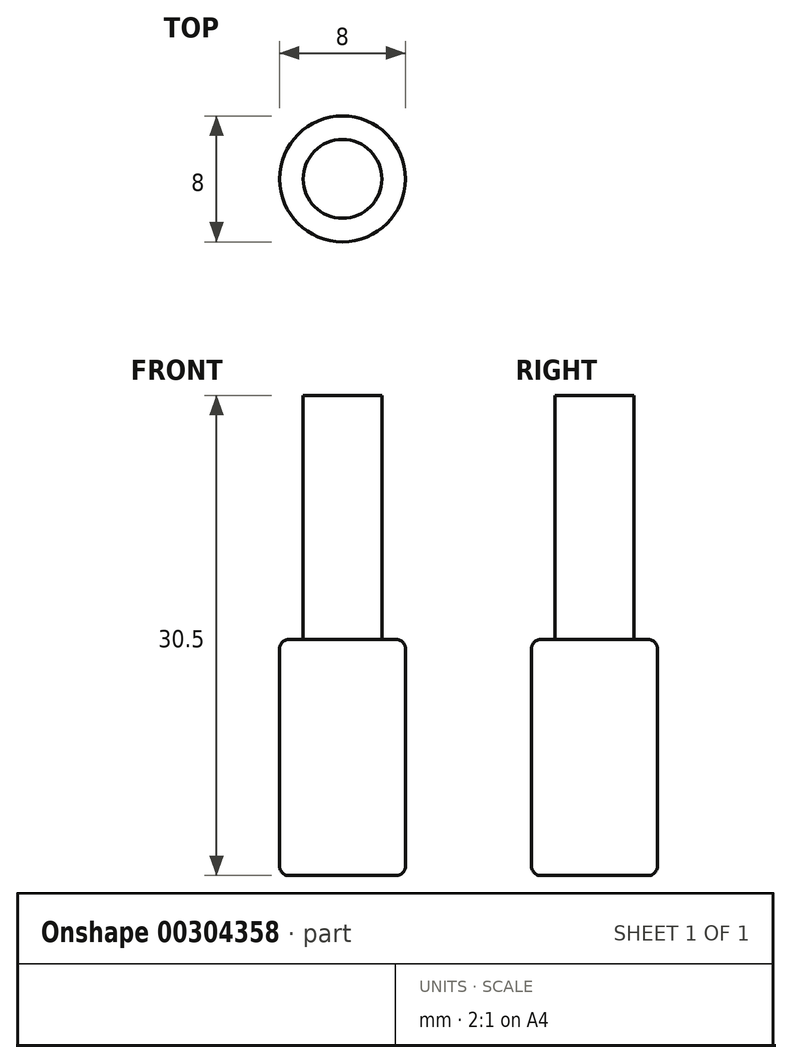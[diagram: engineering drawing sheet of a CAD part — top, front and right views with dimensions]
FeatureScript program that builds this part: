
annotation { "Feature Type Name" : "Feature", "Feature Type Description" : "" }
export const myFeature = defineFeature(function(context is Context, id is Id, definition is map)
    precondition{}
    {
        {
            var Q0;
            Q0=qCreatedBy(makeId("Front.planeOp"),FACE);
            var sketch = newSketch(context, id + "F0", { "sketchPlane" : qUnion([Q0])});
            skLineSegment(sketch, "E0", {"start": v(0, 63.52) * mm, "end": v(0, -56.8) * mm, "construction": true});
            skLineSegment(sketch, "E1", {"start": v(0, 0) * mm, "end": v(4, 0) * mm});
            skLineSegment(sketch, "E2", {"start": v(4, 0) * mm, "end": v(4, 15) * mm});
            skLineSegment(sketch, "E3", {"start": v(4, 15) * mm, "end": v(2.5, 15) * mm});
            skLineSegment(sketch, "E4", {"start": v(2.5, 15) * mm, "end": v(2.5, 30.5) * mm});
            skLineSegment(sketch, "E5", {"start": v(2.5, 30.5) * mm, "end": v(0, 30.5) * mm});
            skLineSegment(sketch, "E6", {"start": v(0, 30.5) * mm, "end": v(0, 0) * mm});
            skSolve(sketch);
        }
        {
            var Q0;
            Q0=makeQuery(id+"F0.imprint","IMPRINT",FACE,{"disambiguationData":[TD([[makeQuery(id+"F0.imprint","IMPRINT",EDGE,{"derivedFrom":sQuery(id+"F0.wireOp",EDGE,"E1")}),1.0]])]});
            var Q1;
            Q1=sQuery(id+"F0.wireOp",EDGE,"E0");
            revolve(context, id + "F1", {"entities" : qUnion([Q0]), "axis" : qUnion([Q1]), "revolveType" : RevolveType.FULL});
        }
        {
            var Q0;
            Q0=makeQuery(id+"F1.opRevolve","SWEPT_EDGE",EDGE,{"disambiguationData":[OSD([sQuery(id+"F0.wireOp",EDGE,"E1"),sQuery(id+"F0.wireOp",EDGE,"E2")])]});
            var Q1;
            Q1=makeQuery(id+"F1.opRevolve","SWEPT_EDGE",EDGE,{"disambiguationData":[OSD([sQuery(id+"F0.wireOp",EDGE,"E2"),sQuery(id+"F0.wireOp",EDGE,"E3")])]});
            fillet(context, id + "F2", {"entities" : qUnion([Q0, Q1]), "radius" : 0.6 * mm, "tangentPropagation" : true, "allowEdgeOverflow" : false});
        }
    });
